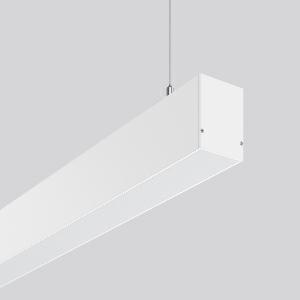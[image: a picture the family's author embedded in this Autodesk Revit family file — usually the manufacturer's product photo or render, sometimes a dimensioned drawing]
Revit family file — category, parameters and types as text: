
# Revit family: less_is_more_50_312321_002_2da9
name_source: partatom
category: Lighting Fixtures
units: mm (PartAtom-declared; Revit-internal decimal feet)

## family parameters
Cut with Voids When Loaded = No
Host = Face
Light Source = No
Part Type = Normal
Room Calculation Point = No
Round Connector Dimension = Use Diameter
Shared = No

## types (1)
- LESS IS MORE 50 (1 x LED Modul 830, 8450 lm, 3000)
    Apparent Load = 74 VA
    CIE Flux Codes = 49 80 96 63 100
    Color Rendering = 80
    Color Temperature = 3000
    Default Elevation = 1800 mm
    Description = Series: LESS IS MORE 50
Linear pendant luminaire for aesthetically sophisticated lighting. Housing: extruded aluminium profile, powder-coated. End cap aluminium powder-coated. Canopy made of aluminium, powder-coated. Diffuser made of non-yellowing plastic (PMMA), opal. Direct 65%, indirect 35% light emission. Suitable for pendant. 2-point steel cable suspension freely positionable and infinitely height-adjustable. Special lengths available on request. LED unit with integrated converter interchangeable and removable. Suitable for through-wiring. With sensors or as a safety luminaire on request. 
Colour: traffic white, matt (RAL 9016)
Length: 1967 mm
Width: 57 mm
Height: 75 mm
Suspension length: 2000 mm
Lamp: LED
Socket: without socket
Colour temperature: 3000K
Colour rendering index (CRI): 80
Light source: LED
Socket lamp2: Without base
Colour temperature: 3000K
System power: 74 W
Rated luminous flux: 8450 lm
Luminous efficiency: 114 lm/W
Control gear: Regulated power supply
Control gear: Regulated power supply
Protection class: I
Type of protection: IP 20
    Height = 75 mm
    Lamp = 1 x LED Modul 830
    Lamp Light Flux = 8450 lm
    Lamp count = 1
    Length = 1967 mm
    Lifetime = 50000 h
    Luminous efficacy = 114 lm/W
    Manufacturer = RZB
    ModVariant = No
    Model = 312321.002
    Mounting Place = Ceiling
    Mounting Type = Pendant
    Number of Poles = 1
    OnlyDefault = Yes
    Power Factor = 1
    Product Name = LESS IS MORE 50
    Product group = Pendant LED linear luminaires
    ProductGroupID = 907
    Protection Class = Protection class I
    Protection Degree = IP 20
    RLX_Detail_Level = 1
    RLX_Emergency_Light_Flux = 0 lm
    RLX_Emergency_Type = 0
    RLX_Emergency_Type_DB = No
    RlxData = <blob elided: 31645 chars, md5=c5d773ef>
    Socket = socket
    Standby Power = 0 W
    System Light Flux = 8450 lm
    System Power = 74 W
    Type Comments = Product without accessories
    Type Image = 312318.002.jpg
    URL = http://relux.com
    VarID = ---
    Voltage = 230 V
    Voltage Range = 220-240 V
    Weight = 0.00 kg
    Width = 57 mm

## geometry (parser evidence)
native form markers: Blend x4, Sweep x12
no freeform markers — native parametric forms only
